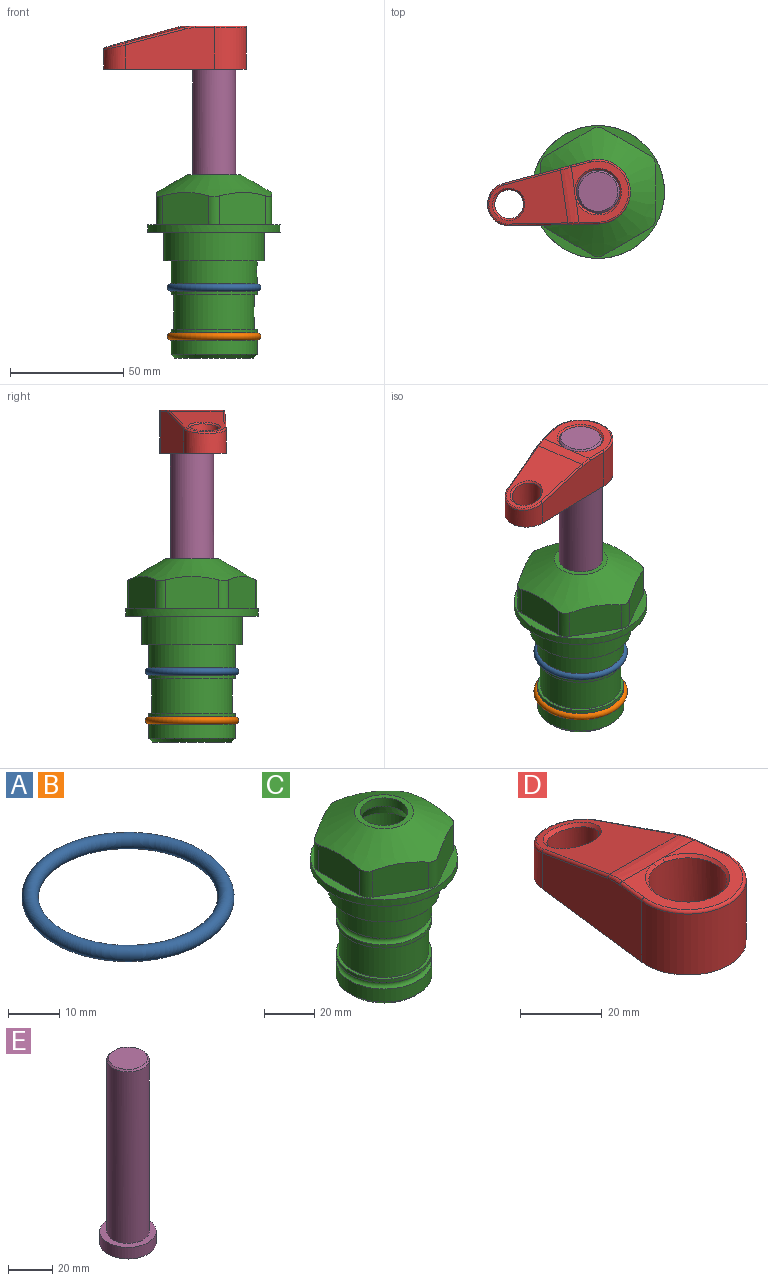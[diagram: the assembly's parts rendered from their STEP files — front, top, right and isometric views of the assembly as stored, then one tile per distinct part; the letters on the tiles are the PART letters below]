
ASSEMBLY  parts=5 mates=4
PART A: 1 faces, bbox 44.7x44.7x3.2 mm
  f0: torus R=19.05mm, axis (0,0,1), area 1193.9mm2
PART B: same geometry as A
PART C: 36 faces, bbox 58.7x58.7x81 mm
  f0: cylinder r=17.78mm len=35.56mm, axis (0,0,1), area 1670.8mm2, adj f23,f24,f31
  f1: cylinder r=19.05mm len=38.1mm, axis (0,0,1), area 1191.9mm2, adj f26,f27,f30
  f2: plane 58.66x58.66mm, normal (0,0,-1), area 1150.6mm2, adj f3,f28
  f3: cylinder r=29.33mm len=58.66mm, axis (0,0,-1), area 585.1mm2, adj f2,f4
  f4: plane 58.66x58.66mm, normal (0,0,1), area 475.9mm2, adj f3,f5,f6,f7,f8,f9,f10,f11
  f5: plane 20.32x14.34mm, normal (-0.5,0.87,0), area 324.4mm2, adj f4,f15,f16,f17
  f6: plane 20.32x14.34mm, normal (0.5,0.87,0), area 324.4mm2, adj f4,f14,f15,f17
  f7: plane 23.48x14.34mm, normal (1,0,0), area 324.4mm2, adj f4,f13,f14,f17
  f8: plane 20.32x14.34mm, normal (0.5,-0.87,0), area 324.4mm2, adj f4,f12,f13,f17
  f9: plane 20.32x14.34mm, normal (-0.5,-0.87,0), area 324.4mm2, adj f4,f11,f12,f17
  f10: plane 23.48x14.34mm, normal (-1,0,0), area 324.4mm2, adj f4,f11,f16,f17
  f11: cylinder r=5.08mm len=12.85mm, axis (0,0,-1), area 67.2mm2, adj f4,f9,f10,f17
  f12: cylinder r=5.08mm len=12.85mm, axis (0,0,-1), area 67.2mm2, adj f4,f8,f9,f17
  f13: cylinder r=5.08mm len=12.85mm, axis (0,0,-1), area 67.2mm2, adj f4,f7,f8,f17
  f14: cylinder r=5.08mm len=12.85mm, axis (0,0,-1), area 67.2mm2, adj f4,f6,f7,f17
  f15: cylinder r=5.08mm len=12.85mm, axis (0,0,-1), area 67.2mm2, adj f4,f5,f6,f17
  f16: cylinder r=5.08mm len=12.85mm, axis (0,0,-1), area 67.2mm2, adj f4,f5,f10,f17
  f17: cone r=11.73mm half-angle=60deg, axis (0,0,-1), area 2071.8mm2, adj f5,f6,f7,f8,f9,f10,f11,f12
  f18: plane 23.46x23.46mm, normal (0,0,1), area 147.4mm2, adj f17,f35
  f19: plane 34.93x34.93mm, normal (0,0,-1), area 958mm2, adj f29
  f20: cylinder r=19.05mm len=38.1mm, axis (0,0,1), area 760.1mm2, adj f21,f29
  f21: torus R=19.05mm, axis (0,0,1), area 565.3mm2, adj f20,f22
  f22: cylinder r=19.05mm len=38.1mm, axis (0,0,1), area 190mm2, adj f21,f23
  f23: plane 38.1x38.1mm, normal (0,0,1), area 146.9mm2, adj f0,f22
  f24: plane 38.1x38.1mm, normal (0,0,-1), area 146.9mm2, adj f0,f25
  f25: cylinder r=19.05mm len=38.1mm, axis (0,0,1), area 190mm2, adj f24,f26
  f26: torus R=19.05mm, axis (0,0,1), area 565.3mm2, adj f1,f25
  f27: plane 44.45x44.45mm, normal (0,0,-1), area 411.7mm2, adj f1,f28
  f28: cylinder r=22.23mm len=44.45mm, axis (0,0,1), area 1773.5mm2, adj f2,f27
  f29: cone r=19.05mm half-angle=45deg, axis (0,0,1), area 257.5mm2, adj f19,f20
  f30: cylinder r=3.17mm len=6.75mm, axis (-1,0,0), area 128mm2, adj f1,f33
  f31: cylinder r=3.17mm len=6.35mm, axis (-1,0,0), area 102.5mm2, adj f0,f33
  f32: plane 25.4x25.4mm, normal (0,0,1), area 506.7mm2, adj f33
  f33: cylinder r=12.7mm len=66.42mm, axis (0,0,-1), area 5236.2mm2, adj f30,f31,f32,f34
  f34: cone r=9.53mm half-angle=30deg, axis (0,0,-1), area 443.4mm2, adj f33,f35
  f35: cylinder r=9.53mm len=19.05mm, axis (0,0,-1), area 240.9mm2, adj f18,f34
PART D: 31 faces, bbox 31.7x65.5x19.8 mm
  f0: plane 39.12x18.26mm, normal (0.99,0.12,0), area 612.2mm2, adj f1,f4,f7,f11,f13,f15
  f1: cylinder r=9.53mm len=18.91mm, axis (0,0,-1), area 296.1mm2, adj f0,f2,f7,f17
  f2: plane 39.12x18.26mm, normal (-0.99,0.12,0), area 612.2mm2, adj f1,f4,f7,f12,f14,f16
  f3: cylinder r=6.35mm len=12.7mm, axis (0,0,-1), area 362.4mm2, adj f7,f18
  f4: cylinder r=14.29mm len=28.58mm, axis (0,0,-1), area 882.2mm2, adj f0,f2,f7,f10
  f5: cylinder r=9.53mm len=19.05mm, axis (0,0,-1), area 1092.6mm2, adj f7,f19,f20
  f6: plane 26.99x23.69mm, normal (0,0,1), area 216.2mm2, adj f9,f10,f11,f12,f19
  f7: plane 63.5x28.58mm, normal (0,0,-1), area 661.8mm2, adj f0,f1,f2,f3,f4,f5,f22,f23
  f8: plane 33.52x23.6mm, normal (0,0.26,0.97), area 486mm2, adj f9,f15,f16,f17,f18
  f9: cylinder r=19.05mm len=24.72mm, axis (1,0,0), area 120.4mm2, adj f6,f8,f13,f14,f20
  f10: torus R=13.49mm, axis (0,0,1), area 59mm2, adj f4,f6,f11,f12
  f11: cylinder r=0.79mm len=8.67mm, axis (0.12,-0.99,0), area 10.8mm2, adj f0,f6,f10,f13
  f12: cylinder r=0.79mm len=8.67mm, axis (0.12,0.99,0), area 10.8mm2, adj f2,f6,f10,f14
  f13: bspline ~4.95x1.42mm, area 6.1mm2, adj f0,f9,f11,f15
  f14: bspline ~4.95x1.42mm, area 6.1mm2, adj f2,f9,f12,f16
  f15: cylinder r=0.79mm len=25.95mm, axis (0.12,-0.96,0.26), area 32.9mm2, adj f0,f8,f13,f17
  f16: cylinder r=0.79mm len=25.95mm, axis (0.12,0.96,-0.26), area 32.9mm2, adj f2,f8,f14,f17
  f17: bspline ~18.91x8.38mm, area 30mm2, adj f1,f8,f15,f16
  f18: bspline ~14.29x14.29mm, area 48.3mm2, adj f3,f8
  f19: cone r=9.53mm half-angle=45deg, axis (0,0,1), area 66.5mm2, adj f5,f6,f20
  f20: bspline ~3.22x0.96mm, area 3.5mm2, adj f5,f9,f19
  f21: plane 2.75x2.72mm, normal (0,0,-1), area 2.9mm2, adj f23,f25,f28
  f22: plane 23.05x15.88mm, normal (-0.99,-0.12,0), area 323.6mm2, adj f7,f25,f26,f27,f28,f29
  f23: plane 23.05x15.88mm, normal (0.99,-0.12,0), area 323.6mm2, adj f7,f21,f25,f27,f28,f30
  f24: cylinder r=9.53mm len=10.69mm, axis (0,0,-1), area 114.7mm2, adj f7,f27,f29,f30
  f25: cylinder r=12.7mm len=20.59mm, axis (0,0,-1), area 381.1mm2, adj f7,f21,f22,f23,f26,f28
  f26: plane 2.75x2.72mm, normal (0,0,-1), area 2.9mm2, adj f22,f25,f28
  f27: plane 19.72x18.37mm, normal (0,-0.26,-0.97), area 291.8mm2, adj f22,f23,f24,f28,f29,f30
  f28: cylinder r=15.88mm len=19.92mm, axis (1,0,0), area 54.8mm2, adj f21,f22,f23,f25,f26,f27
  f29: cylinder r=1.59mm len=11mm, axis (0,0,-1), area 34.7mm2, adj f7,f22,f24,f27
  f30: cylinder r=1.59mm len=11mm, axis (0,0,-1), area 34.7mm2, adj f7,f23,f24,f27
PART E: 6 faces, bbox 25.4x25.4x101.6 mm
  f0: plane 17.46x17.46mm, normal (0,0,1), area 239.5mm2, adj f5
  f1: plane 25.4x25.4mm, normal (0,0,-1), area 506.7mm2, adj f2
  f2: cylinder r=12.7mm len=25.4mm, axis (0,0,1), area 506.7mm2, adj f1,f3
  f3: plane 25.4x25.4mm, normal (0,0,1), area 221.7mm2, adj f2,f4
  f4: cylinder r=9.53mm len=94.46mm, axis (0,0,1), area 5653mm2, adj f3,f5
  f5: cone r=8.73mm half-angle=45deg, axis (0,0,-1), area 64.4mm2, adj f0,f4
PLACE A at identity
PLACE B t=(0,0,-21.59)mm
PLACE C at identity fixed
PLACE D rot(axis=(0,0,1),98deg) t=(0,0,27.55)mm
PLACE E rot(axis=(0,0,1),98deg) t=(0,0,27.55)mm
MATE cylindrical E.f2 <-> C.f0  axis (0,0,-1) through (0,0,-10.55)mm
MATE fastened C.f0 <-> B.f0  axis (0,0,1) through (0,0,-46.1)mm
MATE fastened E.f2 <-> D.f4  axis (0,0,1) through (0,0,91.05)mm
MATE fastened C.f0 <-> A.f0  axis (0,0,1) through (0,0,-24.51)mm
